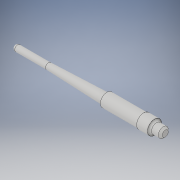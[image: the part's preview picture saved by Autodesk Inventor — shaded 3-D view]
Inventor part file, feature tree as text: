
AUTODESK INVENTOR PART (.ipt)
format: ipt  version: 2018.3 (Build 223284000, 284)  size: 141,824 bytes
history: native  units: in
note: dims shown in document units (in); Inventor stores cm internally (conversion verified against a paired STEP export)
features: revolve x1, sketch x1
ambient origin geometry x8: Origin, YZ Plane, XZ Plane, XY Plane, X Axis, Y Axis, Z Axis, Center Point
bodies: Solid1 (feature_tree)
feature tree (2):
  revolve  "Revolution1"  [1 undecoded]
  sketch  "Sketch1"  dims[d0=0.076in d1=0.165in d3=0.108in d4=0.165in d5=0.56in d6=0.1in d7=0.0765in d9=2.296in d10=0.0455in d13=0.091in d14=0.01in d15=0.005in d16=0.03in d17=0.03in d18=0.03in d19=90.0deg]
note: 1 required parameter value undecoded (feature->parameter linkage not recoverable at this tier; creation-order binding heuristic only, values carry confidence <= 0.55)
